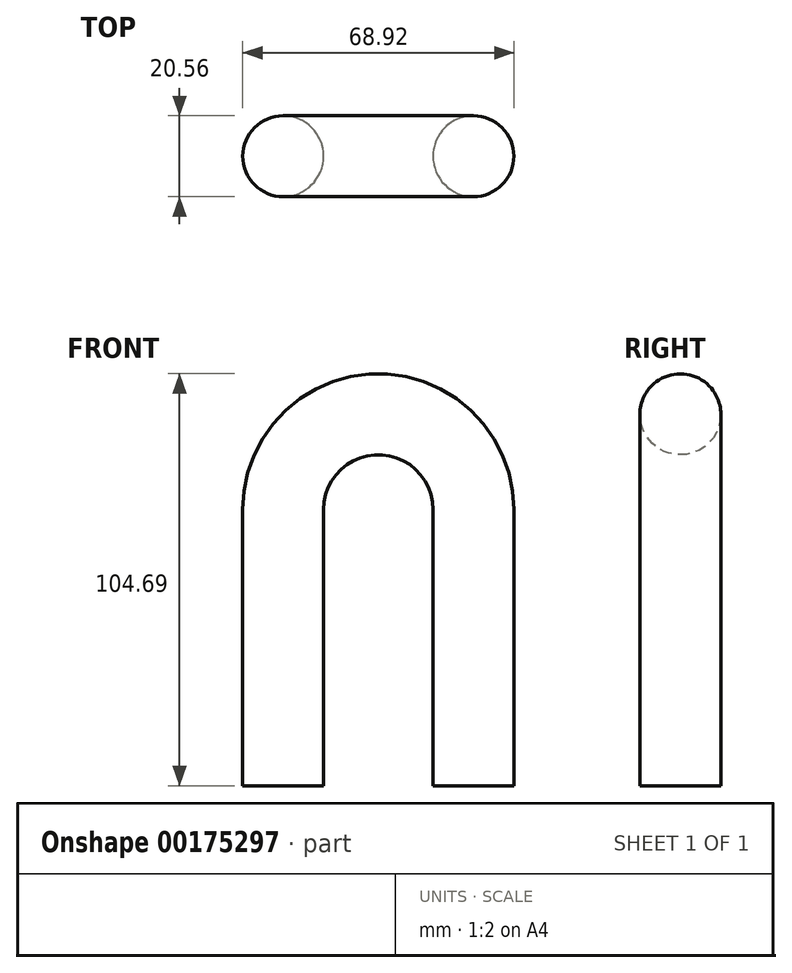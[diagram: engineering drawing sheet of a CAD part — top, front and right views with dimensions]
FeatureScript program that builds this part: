
annotation { "Feature Type Name" : "Feature", "Feature Type Description" : "" }
export const myFeature = defineFeature(function(context is Context, id is Id, definition is map)
    precondition{}
    {
        {
            var Q0;
            Q0=qCreatedBy(makeId("Front.planeOp"),FACE);
            var sketch = newSketch(context, id + "F0", { "sketchPlane" : qUnion([Q0])});
            skLineSegment(sketch, "E0.left", {"start": v(-26.9, -19.86) * mm, "end": v(-26.9, 50.37) * mm});
            skLineSegment(sketch, "E0.right", {"start": v(22.02, -19.86) * mm, "end": v(22.02, 50.37) * mm});
            skArc(sketch, "E1", {"start": v(22.02, 50.37) * mm, "mid": v(-2.45, 74.83) * mm, "end": v(-26.9, 50.37) * mm});
            skSolve(sketch);
        }
        {
            var Q0;
            Q0=qCreatedBy(makeId("Top.planeOp"),FACE);
            var sketch = newSketch(context, id + "F1", { "sketchPlane" : qUnion([Q0])});
            skPoint(sketch, "E2.center.orphan", {"position": v(-27.2, 0) * mm});
            skCircle(sketch, "E3", {"center": v(21.73, 0) * mm, "radius": 10.28 * mm});
            skSolve(sketch);
        }
        {
            var Q0;
            Q0=makeQuery(id+"F1.imprint","IMPRINT",FACE,{"disambiguationData":[TD([[makeQuery(id+"F1.imprint","IMPRINT",EDGE,{"derivedFrom":sQuery(id+"F1.wireOp",EDGE,"E3")}),1.0]])]});
            var Q1;
            Q1=sQuery(id+"F0.wireOp",EDGE,"E1");
            var Q2;
            Q2=sQuery(id+"F0.wireOp",EDGE,"E0.left");
            var Q3;
            Q3=sQuery(id+"F0.wireOp",EDGE,"E0.right");
            sweep(context, id + "F2", {"profiles" : qUnion([Q0]), "path" : qUnion([Q1, Q2, Q3])});
        }
    });
